# Revit family: Medical_Equipment-Workstation-Midmark_Medical-6219_Flat_Panel_Secure_PC_Workstation+Mouse_Trayp
name_source: partatom
category: Specialty Equipment
revit_build: Autodesk Revit 2018 (Build: 20190510_1515(x64)
units: mm (PartAtom-declared; Revit-internal decimal feet)

## family parameters
Always vertical = Yes
Cut with Voids When Loaded = No
OmniClass Number = 23.40.70.11.14.11
OmniClass Title = Medical Equipment
Part Type = Normal
Room Calculation Point = No
Round Connector Dimension = Use Diameter
Shared = No
Work Plane-Based = No

## types (1)
- 6219 - Base Model
    Apparent Load = 150 VA
    Assembly Code = E1020800
    Battery Life = 10 hours
    Cost = 0 $
    Description = Flat Panel Secure PC Workstation + Mouse Tray
    Electrical Amperage = 0 A
    Frequency = 60 Hz
    Manufacturer = Midmark® Medical
    Model = 6219 Flat Panel Secure PC Workstation + Mouse Tray
    Number of Poles = 1
    Product Documentation Link = https://www.midmark.com
    Product Page URL = https://www.midmark.com
    Product data url = https://www.bimobject.com
    URL = https://www.midmark.com
    Voltage = 120 V
    Workstation Top Material = Wood - Midmark - Dark Walnut

## geometry (parser evidence)
native form markers: Blend x12, Sweep x38
no freeform markers — native parametric forms only
